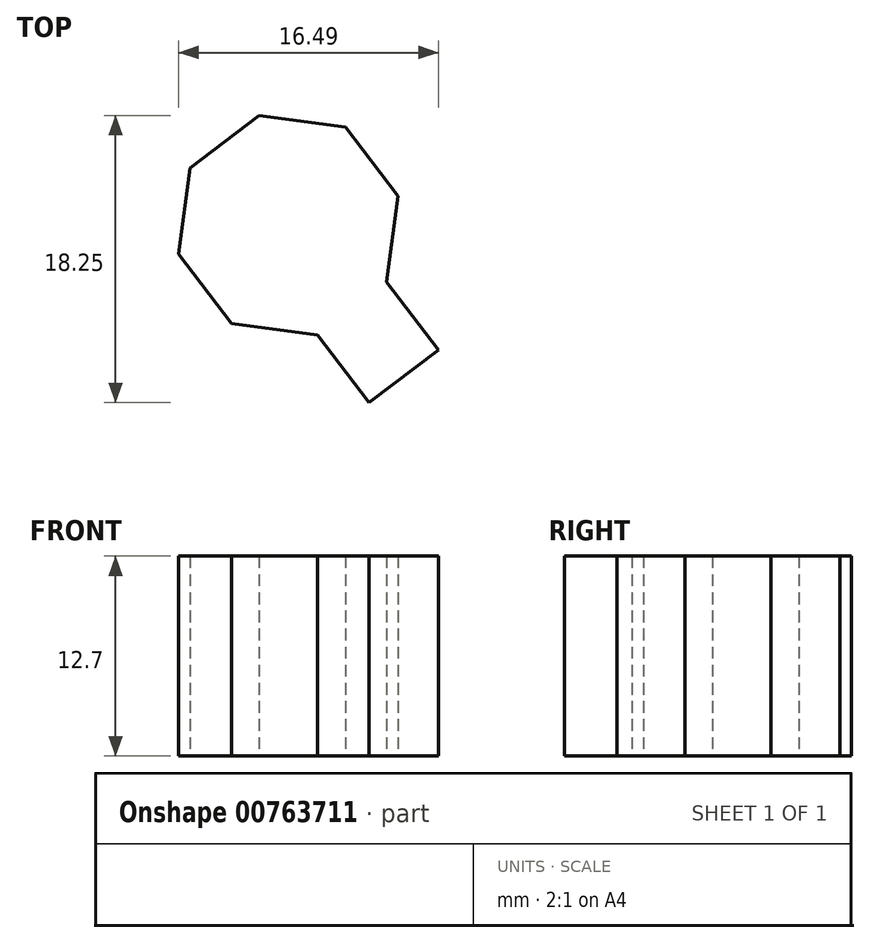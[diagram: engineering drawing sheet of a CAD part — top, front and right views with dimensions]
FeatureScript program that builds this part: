
annotation { "Feature Type Name" : "Feature", "Feature Type Description" : "" }
export const myFeature = defineFeature(function(context is Context, id is Id, definition is map)
    precondition{}
    {
        {
            var Q0;
            Q0=qCreatedBy(makeId("Top.planeOp"),FACE);
            var sketch = newSketch(context, id + "F0", { "sketchPlane" : qUnion([Q0])});
            skCircle(sketch, "E0.cCircle", {"center": v(-16.47, 5.44) * mm, "radius": 7.21 * mm, "construction": true});
            skLineSegment(sketch, "E0.0", {"start": v(-10.24, 1.82) * mm, "end": v(-14.62, -1.53) * mm});
            skLineSegment(sketch, "E0.1", {"start": v(-14.62, -1.53) * mm, "end": v(-20.1, -0.8) * mm});
            skLineSegment(sketch, "E0.2", {"start": v(-20.1, -0.8) * mm, "end": v(-23.44, 3.6) * mm});
            skLineSegment(sketch, "E0.3", {"start": v(-23.44, 3.6) * mm, "end": v(-22.7, 9.06) * mm});
            skLineSegment(sketch, "E0.4", {"start": v(-22.7, 9.06) * mm, "end": v(-18.32, 12.41) * mm});
            skLineSegment(sketch, "E0.5", {"start": v(-18.32, 12.41) * mm, "end": v(-12.85, 11.68) * mm});
            skLineSegment(sketch, "E0.6", {"start": v(-12.85, 11.68) * mm, "end": v(-9.5, 7.29) * mm});
            skLineSegment(sketch, "E0.7", {"start": v(-9.5, 7.29) * mm, "end": v(-10.24, 1.82) * mm});
            skLineSegment(sketch, "E1", {"start": v(-14.62, -1.53) * mm, "end": v(-11.34, -5.84) * mm});
            skLineSegment(sketch, "E2", {"start": v(-11.34, -5.84) * mm, "end": v(-6.95, -2.49) * mm});
            skLineSegment(sketch, "E3", {"start": v(-6.95, -2.49) * mm, "end": v(-10.24, 1.82) * mm});
            skSolve(sketch);
        }
        {
            var Q0;
            Q0 = qSketchRegion(id + "F0", true);
            extrude(context, id + "F1", {"entities" : qUnion([Q0]), "depth" : 12.7 * mm, "offsetDistance" : 25.4 * mm});
        }
    });
